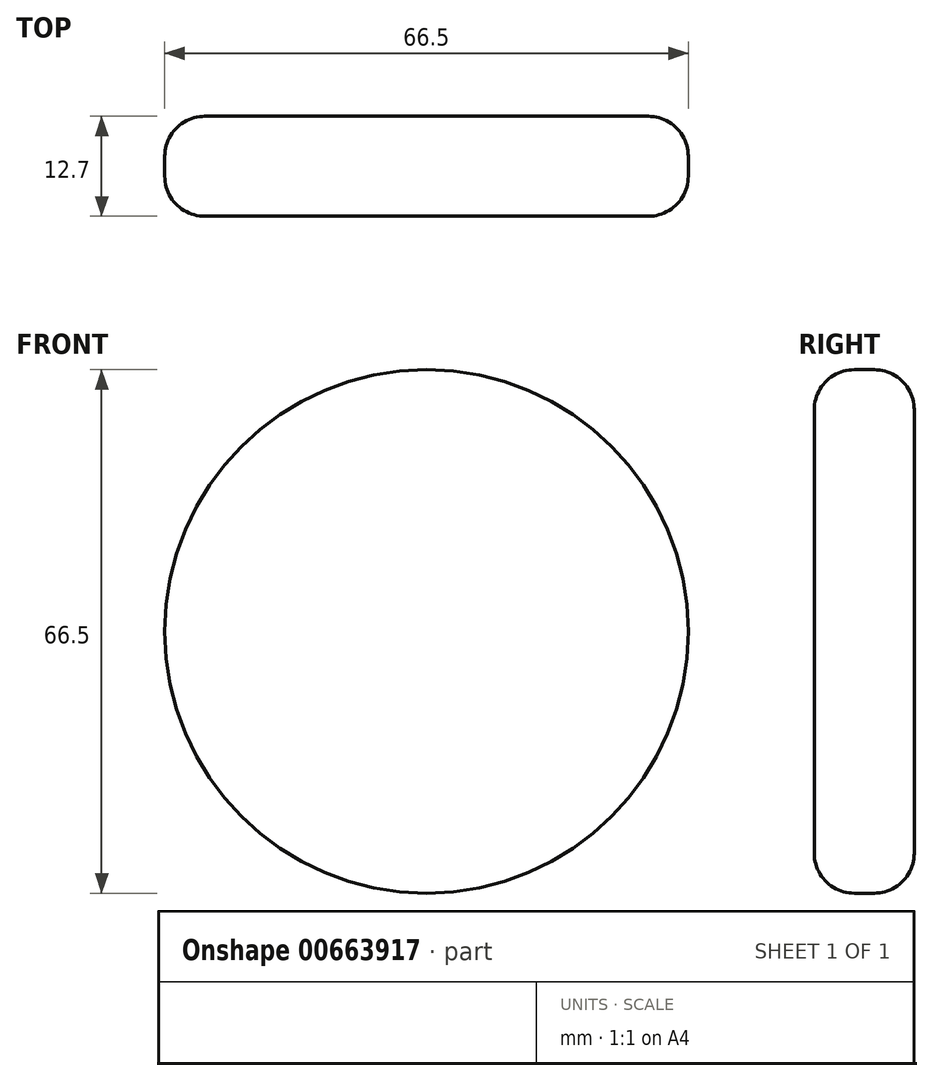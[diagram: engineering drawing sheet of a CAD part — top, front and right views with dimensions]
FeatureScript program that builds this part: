
annotation { "Feature Type Name" : "Feature", "Feature Type Description" : "" }
export const myFeature = defineFeature(function(context is Context, id is Id, definition is map)
    precondition{}
    {
        {
            var Q0;
            Q0=qCreatedBy(makeId("Front.planeOp"),FACE);
            var sketch = newSketch(context, id + "F0", { "sketchPlane" : qUnion([Q0])});
            skCircle(sketch, "E0", {"center": v(-138.74, 32.8) * mm, "radius": 19.17 * mm});
            skSolve(sketch);
        }
        {
            var Q0;
            Q0 = qSketchRegion(id + "F0", true);
            extrude(context, id + "F1", {"entities" : qUnion([Q0]), "depth" : 12.7 * mm, "offsetDistance" : 25.4 * mm});
        }
        {
            var Q0;
            Q0=makeQuery(id+"F1.opExtrude","CAP_EDGE",EDGE,{"disambiguationData":[OSD([sQuery(id+"F0.wireOp",EDGE,"E0")])],"isStart":false});
            var Q1;
            Q1=makeQuery(id+"F1.opExtrude","CAP_EDGE",EDGE,{"disambiguationData":[OSD([sQuery(id+"F0.wireOp",EDGE,"E0")])],"isStart":true});
            fillet(context, id + "F2", {"entities" : qUnion([Q0, Q1]), "radius" : 5.08 * mm, "tangentPropagation" : true, "allowEdgeOverflow" : false});
        }
        {
            var Q0;
            Q0=makeQuery(id+"F1.opExtrude","SWEPT_BODY",BODY,{"disambiguationData":[OSD([sQuery(id+"F0.wireOp",EDGE,"E0")])]});
            deleteBodies(context, id + "F3", {"entities" : qUnion([Q0])});
        }
        {
            var Q0;
            Q0=qCreatedBy(makeId("Front.planeOp"),FACE);
            var sketch = newSketch(context, id + "F4", { "sketchPlane" : qUnion([Q0])});
            skCircle(sketch, "E1", {"center": v(-43.4, 44.02) * mm, "radius": 33.25 * mm});
            skSolve(sketch);
        }
        {
            var Q0;
            Q0 = qSketchRegion(id + "F4", true);
            extrude(context, id + "F5", {"entities" : qUnion([Q0]), "depth" : 12.7 * mm, "offsetDistance" : 25.4 * mm});
        }
        {
            var Q0;
            Q0=makeQuery(id+"F5.opExtrude","CAP_EDGE",EDGE,{"disambiguationData":[OSD([sQuery(id+"F4.wireOp",EDGE,"E1")])],"isStart":true});
            var Q1;
            Q1=makeQuery(id+"F5.opExtrude","CAP_EDGE",EDGE,{"disambiguationData":[OSD([sQuery(id+"F4.wireOp",EDGE,"E1")])],"isStart":false});
            fillet(context, id + "F6", {"entities" : qUnion([Q0, Q1]), "radius" : 5.08 * mm, "tangentPropagation" : true, "allowEdgeOverflow" : false});
        }
    });
